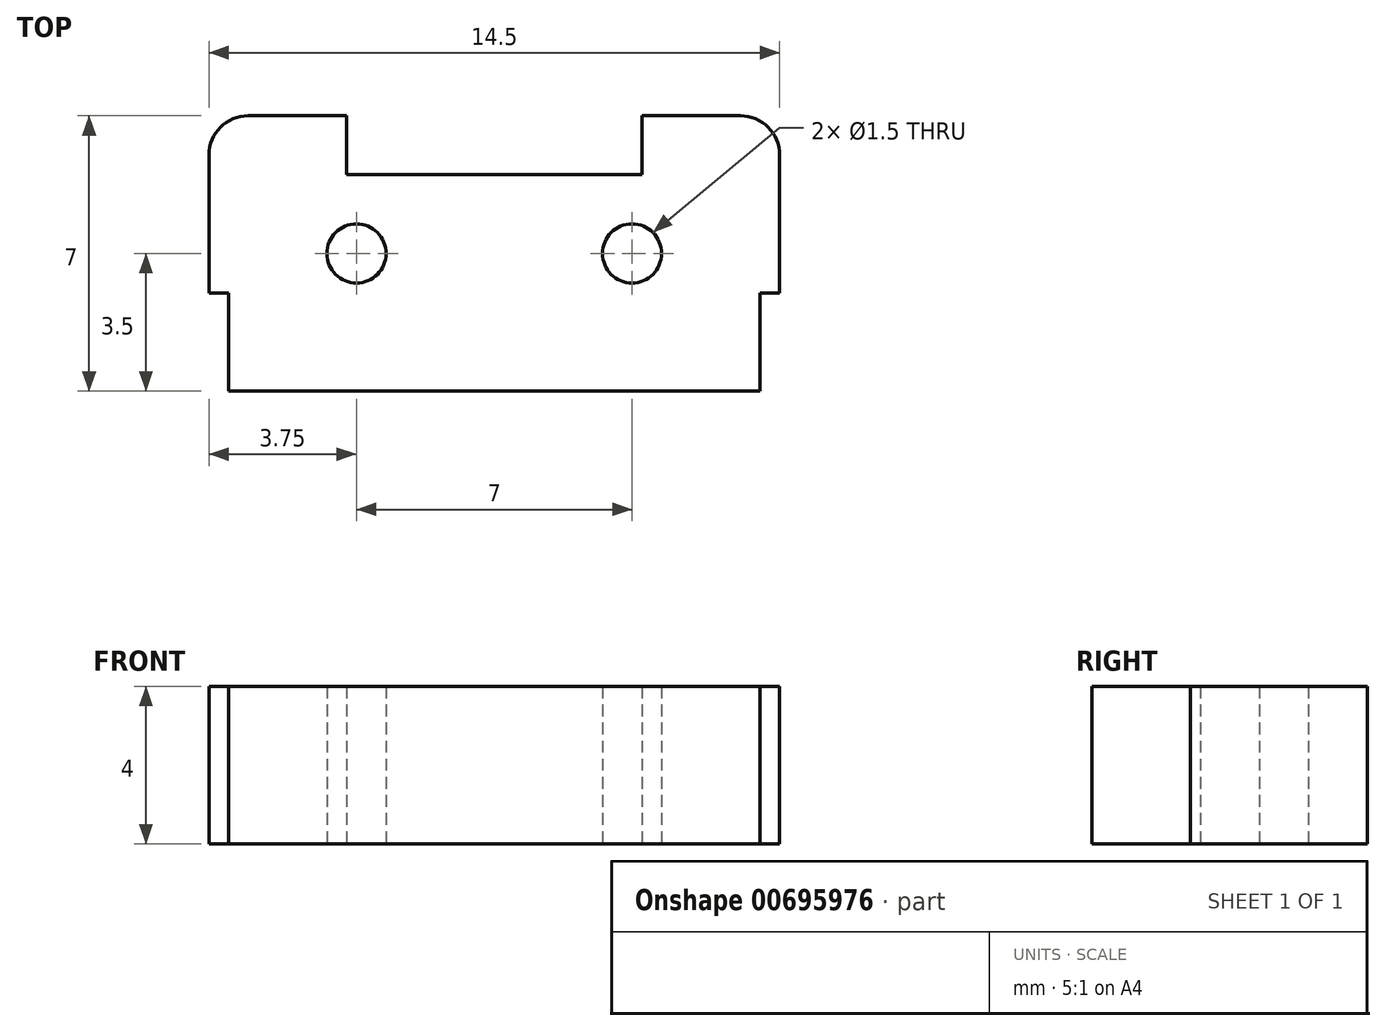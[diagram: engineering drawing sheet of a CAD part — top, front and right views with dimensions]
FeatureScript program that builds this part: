
annotation { "Feature Type Name" : "Feature", "Feature Type Description" : "" }
export const myFeature = defineFeature(function(context is Context, id is Id, definition is map)
    precondition{}
    {
        {
            var Q0;
            Q0=qCreatedBy(makeId("Top.planeOp"),FACE);
            var sketch = newSketch(context, id + "F0", { "sketchPlane" : qUnion([Q0])});
            skLineSegment(sketch, "E0.bottom", {"start": v(0, 0) * mm, "end": v(14.5, 0) * mm});
            skLineSegment(sketch, "E0.top", {"start": v(0, 7) * mm, "end": v(14.5, 7) * mm});
            skLineSegment(sketch, "E0.left", {"start": v(0, 0) * mm, "end": v(0, 7) * mm});
            skLineSegment(sketch, "E0.right", {"start": v(14.5, 0) * mm, "end": v(14.5, 7) * mm});
            skLineSegment(sketch, "E1.bottom", {"start": v(0, 2.5) * mm, "end": v(0.5, 2.5) * mm});
            skLineSegment(sketch, "E1.top", {"start": v(0, 0) * mm, "end": v(0.5, 0) * mm});
            skLineSegment(sketch, "E1.left", {"start": v(0, 2.5) * mm, "end": v(0, 0) * mm});
            skLineSegment(sketch, "E1.right", {"start": v(0.5, 2.5) * mm, "end": v(0.5, 0) * mm});
            skLineSegment(sketch, "E2.1.0.0", {"start": v(14, 2.5) * mm, "end": v(14, 0) * mm});
            skLineSegment(sketch, "E2.1.0.1", {"start": v(14.5, 2.5) * mm, "end": v(14.5, 0) * mm});
            skLineSegment(sketch, "E2.1.0.2", {"start": v(14, 2.5) * mm, "end": v(14.5, 2.5) * mm});
            skLineSegment(sketch, "E2.direction1", {"start": v(0, 0) * mm, "end": v(14, 0) * mm, "construction": true});
            skCircle(sketch, "E3", {"center": v(1, 6) * mm, "radius": 1 * mm});
            skCircle(sketch, "E4.1.0.0", {"center": v(13.5, 6) * mm, "radius": 1 * mm});
            skLineSegment(sketch, "E4.direction1", {"start": v(1, 6) * mm, "end": v(13.5, 6) * mm, "construction": true});
            skLineSegment(sketch, "E5.bottom", {"start": v(3.5, 7) * mm, "end": v(11, 7) * mm});
            skLineSegment(sketch, "E5.top", {"start": v(3.5, 5.5) * mm, "end": v(11, 5.5) * mm});
            skLineSegment(sketch, "E5.left", {"start": v(3.5, 7) * mm, "end": v(3.5, 5.5) * mm});
            skLineSegment(sketch, "E5.right", {"start": v(11, 7) * mm, "end": v(11, 5.5) * mm});
            skCircle(sketch, "E6", {"center": v(3.75, 3.5) * mm, "radius": 0.75 * mm});
            skCircle(sketch, "E7.1.0.0", {"center": v(10.75, 3.5) * mm, "radius": 0.75 * mm});
            skLineSegment(sketch, "E7.direction1", {"start": v(3.75, 3.5) * mm, "end": v(10.75, 3.5) * mm, "construction": true});
            skSolve(sketch);
        }
        {
            var Q0;
            {var subQ0=sQuery(id+"F0.wireOp",EDGE,"E3");var subQ1=makeQuery(id+"F0.imprint","INTERSECT",VERTEX,{"derivedFrom":[sQuery(id+"F0.wireOp",EDGE,"E0.top"),subQ0]});Q0=makeQuery(id+"F0.imprint","IMPRINT",FACE,{"disambiguationData":[TD([[makeQuery(id+"F0.imprint","IMPRINT",EDGE,{"disambiguationData":[TD([[subQ1,-1.0]])],"derivedFrom":subQ0}),1.0]])]});}
            var Q1;
            {var subQ8=sQuery(id+"F0.wireOp",EDGE,"E1.bottom");Q1=makeQuery(id+"F0.imprint","IMPRINT",FACE,{"disambiguationData":[TD([[makeQuery(id+"F0.imprint","IMPRINT",EDGE,{"derivedFrom":subQ8}),1.0]])]});}
            var Q2;
            {var subQ0=sQuery(id+"F0.wireOp",EDGE,"E4.1.0.0");var subQ1=makeQuery(id+"F0.imprint","INTERSECT",VERTEX,{"derivedFrom":[sQuery(id+"F0.wireOp",EDGE,"E0.top"),subQ0]});Q2=makeQuery(id+"F0.imprint","IMPRINT",FACE,{"disambiguationData":[TD([[makeQuery(id+"F0.imprint","IMPRINT",EDGE,{"disambiguationData":[TD([[subQ1,1.0]])],"derivedFrom":subQ0}),1.0]])]});}
            extrude(context, id + "F1", {"entities" : qUnion([Q0, Q1, Q2]), "depth" : 4 * mm, "offsetDistance" : 25 * mm});
        }
    });
